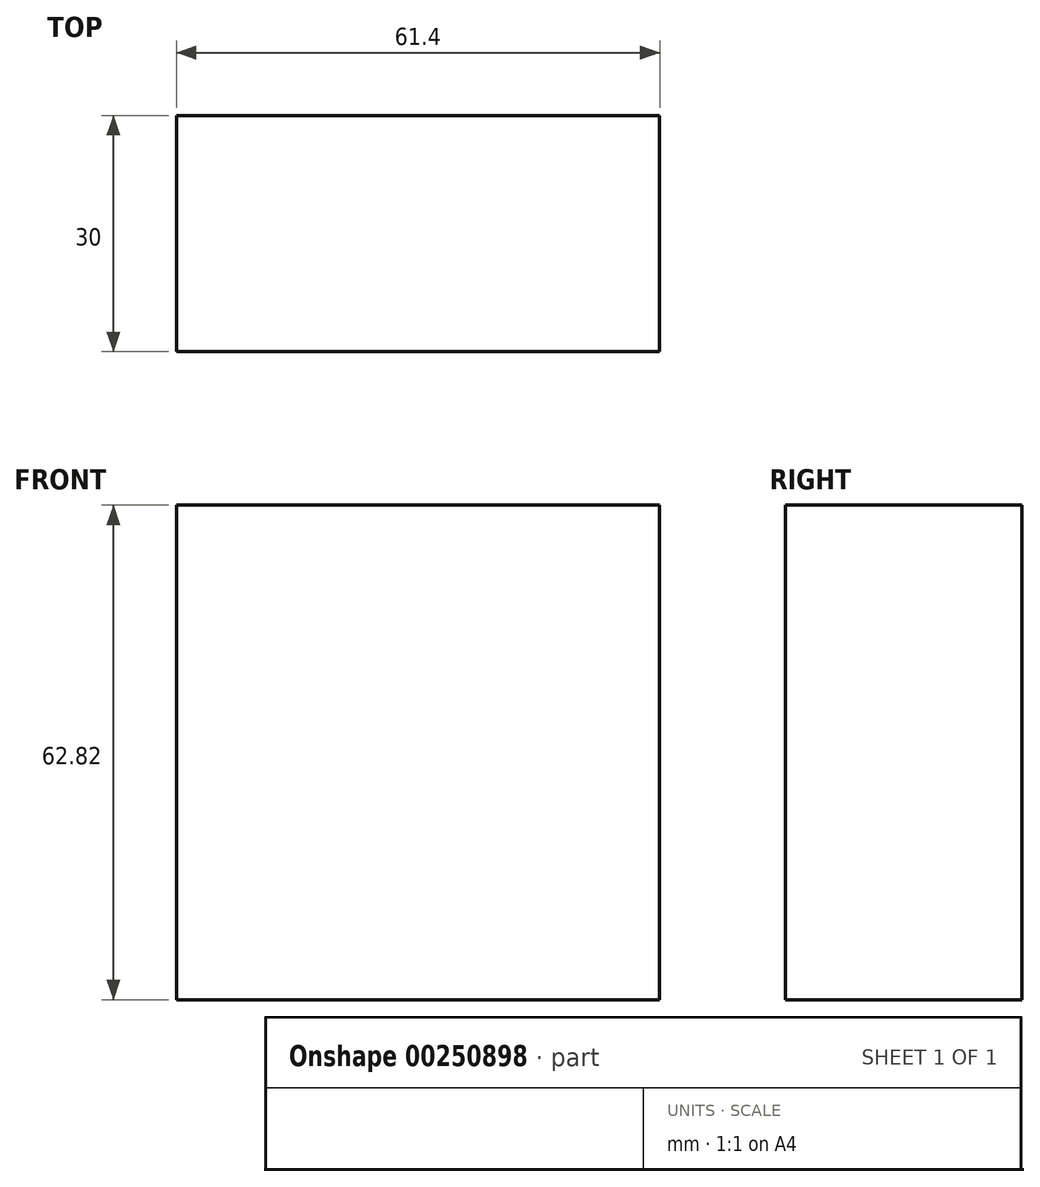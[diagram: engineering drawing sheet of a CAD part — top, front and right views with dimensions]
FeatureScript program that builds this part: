
annotation { "Feature Type Name" : "Feature", "Feature Type Description" : "" }
export const myFeature = defineFeature(function(context is Context, id is Id, definition is map)
    precondition{}
    {
        {
            var Q0;
            Q0=qCreatedBy(makeId("Front.planeOp"),FACE);
            var sketch = newSketch(context, id + "F0", { "sketchPlane" : qUnion([Q0])});
            skLineSegment(sketch, "E0.bottom", {"start": v(30.7, -31.41) * mm, "end": v(-30.7, -31.41) * mm});
            skLineSegment(sketch, "E0.top", {"start": v(30.7, 31.41) * mm, "end": v(-30.7, 31.41) * mm});
            skLineSegment(sketch, "E0.left", {"start": v(30.7, -31.41) * mm, "end": v(30.7, 31.41) * mm});
            skLineSegment(sketch, "E0.right", {"start": v(-30.7, -31.41) * mm, "end": v(-30.7, 31.41) * mm});
            skPoint(sketch, "E0.middle", {"position": v(0, 0) * mm});
            skSolve(sketch);
        }
        {
            var Q0;
            Q0=makeQuery(id+"F0.imprint","IMPRINT",FACE,{"disambiguationData":[TD([[makeQuery(id+"F0.imprint","IMPRINT",EDGE,{"derivedFrom":sQuery(id+"F0.wireOp",EDGE,"E0.bottom")}),-1.0]])]});
            extrude(context, id + "F1", {"entities" : qUnion([Q0]), "endBound" : BoundingType.SYMMETRIC, "depth" : 30 * mm});
        }
    });
